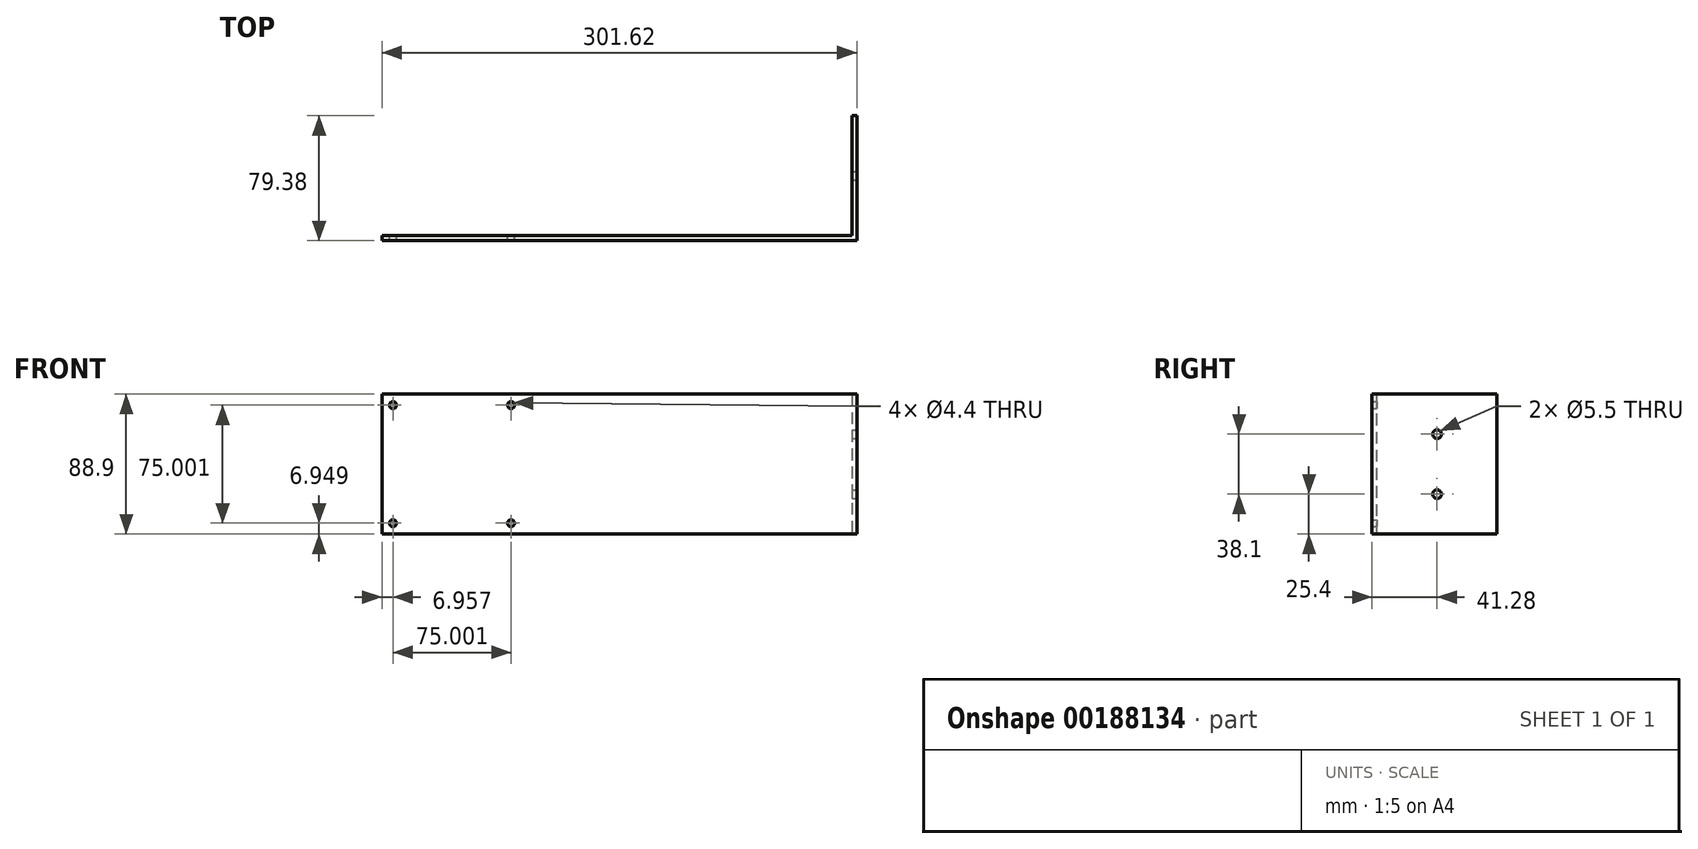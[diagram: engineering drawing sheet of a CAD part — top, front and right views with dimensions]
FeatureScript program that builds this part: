
annotation { "Feature Type Name" : "Feature", "Feature Type Description" : "" }
export const myFeature = defineFeature(function(context is Context, id is Id, definition is map)
    precondition{}
    {
        {
            var Q0;
            Q0=qCreatedBy(makeId("Front.planeOp"),FACE);
            var sketch = newSketch(context, id + "F0", { "sketchPlane" : qUnion([Q0])});
            skLineSegment(sketch, "E0.bottom", {"start": v(-150.81, -44.45) * mm, "end": v(150.81, -44.45) * mm});
            skLineSegment(sketch, "E0.top", {"start": v(-150.81, 44.45) * mm, "end": v(150.81, 44.45) * mm});
            skLineSegment(sketch, "E0.left", {"start": v(-150.81, -44.45) * mm, "end": v(-150.81, 44.45) * mm});
            skLineSegment(sketch, "E0.right", {"start": v(150.81, -44.45) * mm, "end": v(150.81, 44.45) * mm});
            skPoint(sketch, "E0.middle", {"position": v(0, 0) * mm});
            skLineSegment(sketch, "E1.bottom", {"start": v(-68.85, -37.5) * mm, "end": v(-143.85, -37.5) * mm});
            skLineSegment(sketch, "E1.top", {"start": v(-68.85, 37.5) * mm, "end": v(-143.85, 37.5) * mm});
            skLineSegment(sketch, "E1.left", {"start": v(-68.85, -37.5) * mm, "end": v(-68.85, 37.5) * mm});
            skLineSegment(sketch, "E1.right", {"start": v(-143.85, -37.5) * mm, "end": v(-143.85, 37.5) * mm});
            skPoint(sketch, "E1.middle", {"position": v(-106.35, 0) * mm});
            skSolve(sketch);
        }
        {
            var Q0;
            Q0=makeQuery(id+"F0.imprint","IMPRINT",FACE,{"disambiguationData":[TD([[makeQuery(id+"F0.imprint","IMPRINT",EDGE,{"derivedFrom":sQuery(id+"F0.wireOp",EDGE,"E0.bottom")}),1.0]])]});
            var Q1;
            Q1=makeQuery(id+"F0.imprint","IMPRINT",FACE,{"disambiguationData":[TD([[makeQuery(id+"F0.imprint","IMPRINT",EDGE,{"derivedFrom":sQuery(id+"F0.wireOp",EDGE,"E1.bottom")}),-1.0]])]});
            extrude(context, id + "F1", {"entities" : qUnion([Q0, Q1]), "depth" : 3.17 * mm});
        }
        {
            var Q0;
            Q0=sQuery(id+"F0.wireOp",VERTEX,"E1.top.end");
            var Q1;
            Q1=sQuery(id+"F0.wireOp",VERTEX,"E1.top.start");
            var Q2;
            Q2=sQuery(id+"F0.wireOp",VERTEX,"E1.left.start");
            var Q3;
            Q3=sQuery(id+"F0.wireOp",VERTEX,"E1.bottom.end");
            var Q4;
            Q4=makeQuery(id+"F1.opExtrude","SWEPT_BODY",BODY,{"disambiguationData":[OSD([sQuery(id+"F0.wireOp",EDGE,"E0.bottom"),sQuery(id+"F0.wireOp",EDGE,"E0.top"),sQuery(id+"F0.wireOp",EDGE,"E0.left"),sQuery(id+"F0.wireOp",EDGE,"E0.right")])]});
            hole(context, id + "F2", {"style" : HoleStyle.SIMPLE, "endStyle" : HoleEndStyle.THROUGH, "oppositeDirection" : true, "standardTappedOrClearance" : lookupTablePath({ "standard" : "ISO", "fit" : "Normal", "size" : "M4", "type" : "Clearance" }), "standardBlindInLast" : lookupTablePath({ "fit" : "Standard", "standard" : "ISO", "size" : "M4", "type" : "Clearance" }), "holeDiameter" : 4.4 * mm, "startFromSketch" : true, "locations" : qUnion([Q0, Q1, Q2, Q3]), "scope" : qUnion([Q4]), "isTappedThrough" : true});
        }
        {
            var Q0;
            Q0=makeQuery(id+"F0.imprint","IMPRINT",FACE,{"disambiguationData":[TD([[makeQuery(id+"F0.imprint","IMPRINT",EDGE,{"derivedFrom":sQuery(id+"F0.wireOp",EDGE,"E0.bottom")}),1.0]])]});
            var sketch = newSketch(context, id + "F3", { "sketchPlane" : qUnion([Q0])});
            skLineSegment(sketch, "E2", {"start": v(147.64, 45.65) * mm, "end": v(147.64, -45.04) * mm});
            skSolve(sketch);
        }
        {
            var Q0;
            {var subQ5=makeQuery(id+"F0.imprint","IMPRINT",EDGE,{"derivedFrom":sQuery(id+"F0.wireOp",EDGE,"E0.right")});Q0=makeQuery(id+"F3.imprint","IMPRINT",FACE,{"disambiguationData":[TD([[makeQuery(id+"F3.imprint","IMPRINT",EDGE,{"derivedFrom":subQ5}),1.0]])]});}
            extrude(context, id + "F4", {"entities" : qUnion([Q0]), "operationType" : NewBodyOperationType.ADD, "oppositeDirection" : true, "depth" : 76.2 * mm});
        }
        {
            var Q0;
            {var subQ0=sQuery(id+"F0.wireOp",EDGE,"E0.right");Q0=makeQuery(id+"F4.boolean.opBoolean","MERGE",FACE,{"derivedFrom":[makeQuery(id+"F1.opExtrude","SWEPT_FACE",FACE,{"disambiguationData":[OSD([subQ0])]}),makeQuery(id+"F4.opExtrude","SWEPT_FACE",FACE,{"disambiguationData":[OSD([subQ0])]})]});}
            var sketch = newSketch(context, id + "F5", { "sketchPlane" : qUnion([Q0])});
            skCircle(sketch, "E3", {"center": v(38.1, 19.05) * mm, "radius": 1.35 * mm});
            skCircle(sketch, "E4", {"center": v(38.1, -19.05) * mm, "radius": 1.64 * mm});
            skSolve(sketch);
        }
        {
            var Q0;
            Q0=sQuery(id+"F5.wireOp",VERTEX,"E3.center");
            var Q1;
            Q1=sQuery(id+"F5.wireOp",VERTEX,"E4.center");
            var Q2;
            Q2=makeQuery(id+"F1.opExtrude","SWEPT_BODY",BODY,{"disambiguationData":[OSD([sQuery(id+"F0.wireOp",EDGE,"E0.bottom"),sQuery(id+"F0.wireOp",EDGE,"E0.top"),sQuery(id+"F0.wireOp",EDGE,"E0.left"),sQuery(id+"F0.wireOp",EDGE,"E0.right")])]});
            hole(context, id + "F6", {"style" : HoleStyle.SIMPLE, "endStyle" : HoleEndStyle.THROUGH, "standardTappedOrClearance" : lookupTablePath({ "standard" : "ISO", "fit" : "Normal", "size" : "M5", "type" : "Clearance" }), "standardBlindInLast" : lookupTablePath({ "fit" : "Standard", "standard" : "ISO", "size" : "M5", "type" : "Clearance" }), "holeDiameter" : 5.5 * mm, "startFromSketch" : true, "locations" : qUnion([Q0, Q1]), "scope" : qUnion([Q2]), "isTappedThrough" : true});
        }
    });
